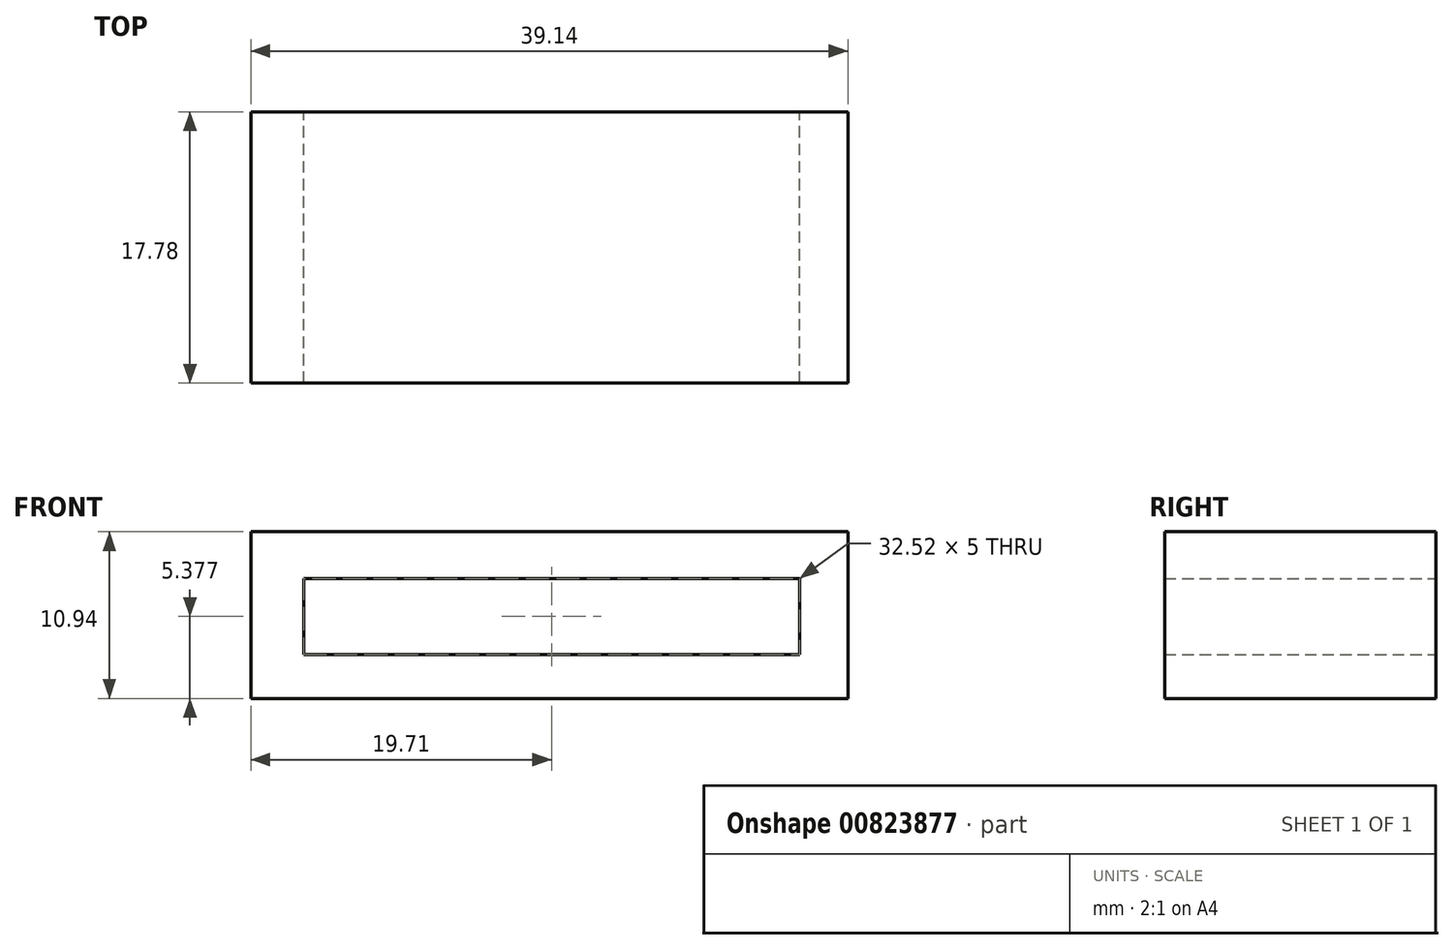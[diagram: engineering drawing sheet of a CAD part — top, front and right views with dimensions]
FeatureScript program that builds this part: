
annotation { "Feature Type Name" : "Feature", "Feature Type Description" : "" }
export const myFeature = defineFeature(function(context is Context, id is Id, definition is map)
    precondition{}
    {
        {
            var Q0;
            Q0=qCreatedBy(makeId("Front.planeOp"),FACE);
            var sketch = newSketch(context, id + "F0", { "sketchPlane" : qUnion([Q0])});
            skLineSegment(sketch, "E0", {"start": v(-18.85, 21.84) * mm, "end": v(13.67, 21.84) * mm});
            skLineSegment(sketch, "E1", {"start": v(13.67, 21.84) * mm, "end": v(-18.85, 21.84) * mm});
            skLineSegment(sketch, "E2.top", {"start": v(-18.85, 16.84) * mm, "end": v(13.67, 16.84) * mm});
            skLineSegment(sketch, "E2.left", {"start": v(-18.85, 21.84) * mm, "end": v(-18.85, 16.84) * mm});
            skLineSegment(sketch, "E2.right", {"start": v(13.67, 21.84) * mm, "end": v(13.67, 16.84) * mm});
            skLineSegment(sketch, "E3.bottom", {"start": v(-22.3, 24.9) * mm, "end": v(16.84, 24.9) * mm});
            skLineSegment(sketch, "E3.top", {"start": v(-22.3, 13.96) * mm, "end": v(16.84, 13.96) * mm});
            skLineSegment(sketch, "E3.left", {"start": v(-22.3, 24.9) * mm, "end": v(-22.3, 13.96) * mm});
            skLineSegment(sketch, "E3.right", {"start": v(16.84, 24.9) * mm, "end": v(16.84, 13.96) * mm});
            skSolve(sketch);
        }
        {
            var Q0;
            Q0 = qSketchRegion(id + "F0", true);
            extrude(context, id + "F1", {"entities" : qUnion([Q0]), "depth" : 17.78 * mm, "offsetDistance" : 25.4 * mm});
        }
    });
